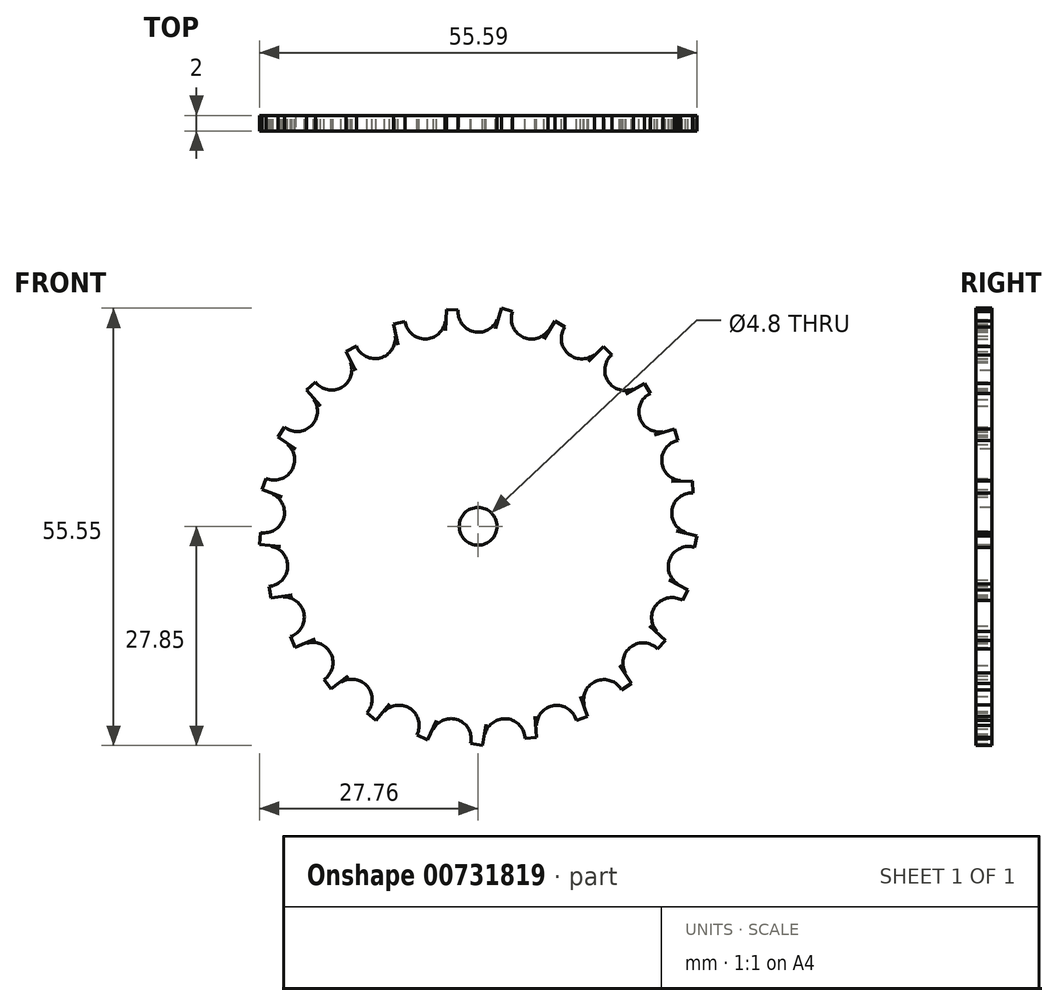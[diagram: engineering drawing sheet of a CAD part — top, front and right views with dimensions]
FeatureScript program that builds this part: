
annotation { "Feature Type Name" : "Feature", "Feature Type Description" : "" }
export const myFeature = defineFeature(function(context is Context, id is Id, definition is map)
    precondition{}
    {
        {
            var Q0;
            Q0=qCreatedBy(makeId("Front.planeOp"),FACE);
            var sketch = newSketch(context, id + "F0", { "sketchPlane" : qUnion([Q0])});
            skArc(sketch, "E0", {"start": v(-24.57, 12.6) * mm, "mid": v(-21.2, 12.75) * mm, "end": v(-20.88, 16.12) * mm});
            skLineSegment(sketch, "E1", {"start": v(-24.57, 12.6) * mm, "end": v(-25.43, 11.37) * mm});
            skLineSegment(sketch, "E2", {"start": v(-25.43, 11.37) * mm, "end": v(-22.14, 9.1) * mm});
            skLineSegment(sketch, "E3", {"start": v(-22.14, 9.1) * mm, "end": v(-18.72, 14.03) * mm});
            skLineSegment(sketch, "E4", {"start": v(-18.72, 14.03) * mm, "end": v(-20.88, 16.12) * mm});
            skCircle(sketch, "E5", {"center": v(0, 0) * mm, "radius": 1.38 * mm});
            skSolve(sketch);
        }
        {
            var Q0;
            Q0=makeQuery(id+"F0.imprint","IMPRINT",FACE,{"disambiguationData":[TD([[makeQuery(id+"F0.imprint","IMPRINT",EDGE,{"derivedFrom":sQuery(id+"F0.wireOp",EDGE,"E0")}),-1.0]])]});
            extrude(context, id + "F1", {"entities" : qUnion([Q0]), "depth" : 2 * mm, "offsetDistance" : 25 * mm});
        }
        {
            var Q0;
            Q0=makeQuery(id+"F1.opExtrude","SWEPT_BODY",BODY,{"disambiguationData":[OSD([sQuery(id+"F0.wireOp",EDGE,"E0"),sQuery(id+"F0.wireOp",EDGE,"E1"),sQuery(id+"F0.wireOp",EDGE,"E2"),sQuery(id+"F0.wireOp",EDGE,"E3"),sQuery(id+"F0.wireOp",EDGE,"E4")])]});
            var Q1;
            Q1=sQuery(id+"F0.wireOp",EDGE,"E5");
            circularPattern(context, id + "F2", {"entities" : qUnion([Q0]), "axis" : qUnion([Q1]), "angle" : 360 * degree, "instanceCount" : 25, "equalSpace" : true, "isCentered" : true});
        }
        {
            var Q0;
            Q0=qSketchRegion(id+"F0",true);
            extrude(context, id + "F3", {"entities" : qUnion([Q0]), "operationType" : NewBodyOperationType.ADD, "depth" : 2 * mm, "offsetDistance" : 25 * mm});
        }
        {
            var Q0;
            Q0=qCreatedBy(makeId("Front.planeOp"),FACE);
            var sketch = newSketch(context, id + "F4", { "sketchPlane" : qUnion([Q0])});
            skCircle(sketch, "E6", {"center": v(0, 0) * mm, "radius": 24.18 * mm});
            skSolve(sketch);
        }
        {
            var Q0;
            Q0=qSketchRegion(id+"F4",true);
            extrude(context, id + "F5", {"entities" : qUnion([Q0]), "operationType" : NewBodyOperationType.ADD, "depth" : 2 * mm, "offsetDistance" : 25 * mm});
        }
        {
            var Q0;
            Q0=qCreatedBy(makeId("Front.planeOp"),FACE);
            var sketch = newSketch(context, id + "F6", { "sketchPlane" : qUnion([Q0])});
            skCircle(sketch, "E7", {"center": v(0, 0) * mm, "radius": 2.4 * mm});
            skSolve(sketch);
        }
        {
            var Q0;
            Q0 = qSketchRegion(id + "F6", true);
            extrude(context, id + "F7", {"entities" : qUnion([Q0]), "operationType" : NewBodyOperationType.REMOVE, "endBound" : BoundingType.SYMMETRIC, "oppositeDirection" : true, "depth" : 25 * mm, "offsetDistance" : 25 * mm});
        }
    });
